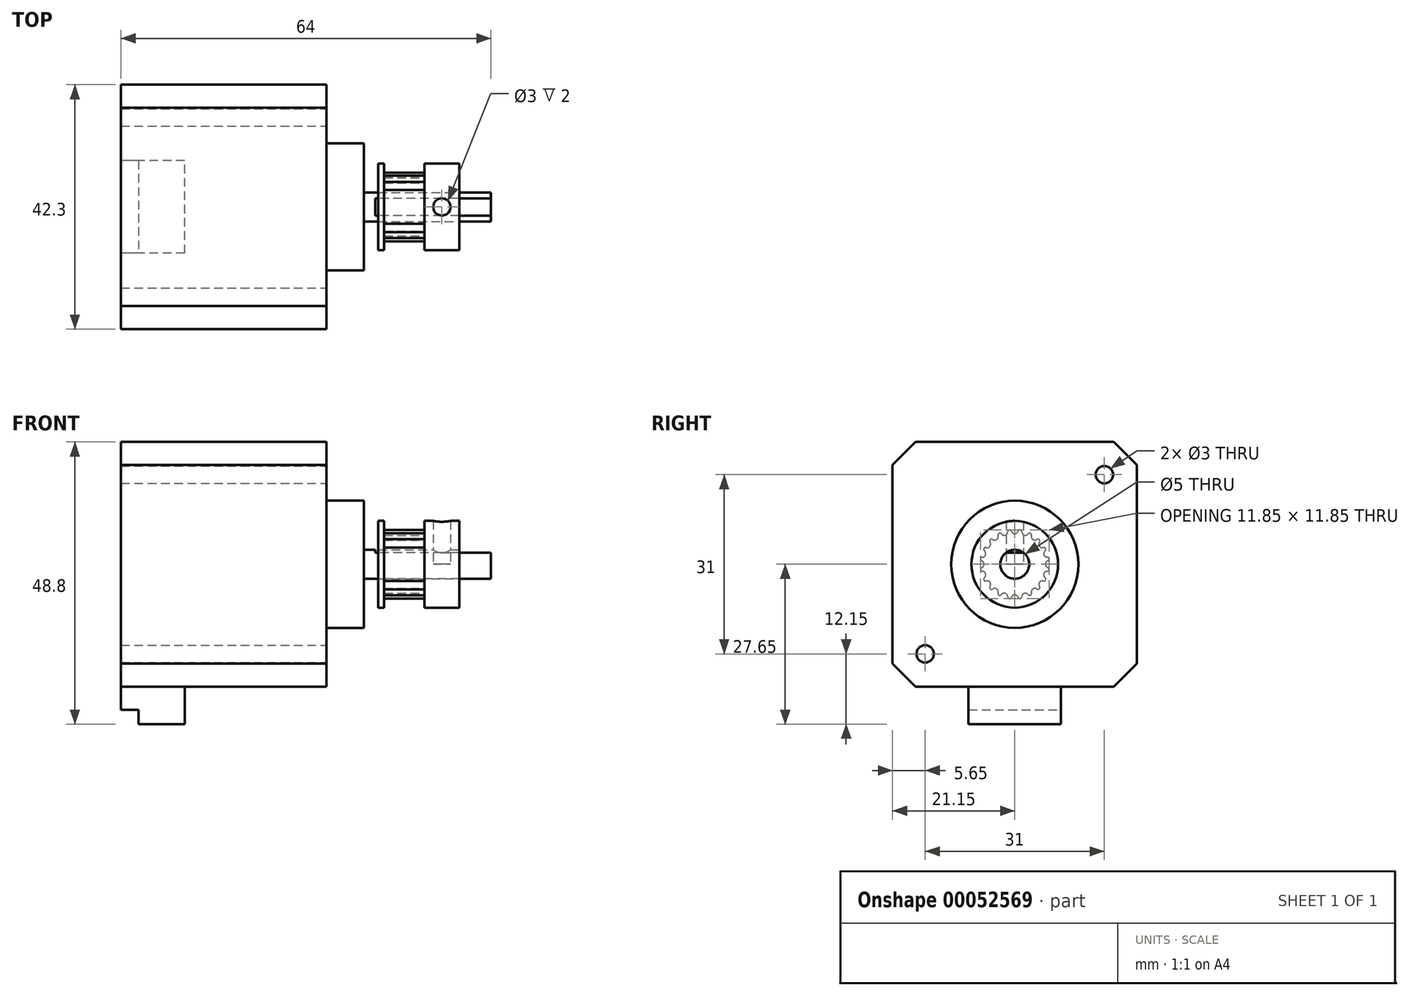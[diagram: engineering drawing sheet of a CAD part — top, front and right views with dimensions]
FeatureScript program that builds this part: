
annotation { "Feature Type Name" : "Feature", "Feature Type Description" : "" }
export const myFeature = defineFeature(function(context is Context, id is Id, definition is map)
    precondition{}
    {
        {
            var Q0;
            Q0=qCreatedBy(makeId("Right.planeOp"),FACE);
            var sketch = newSketch(context, id + "F0", { "sketchPlane" : qUnion([Q0])});
            skLineSegment(sketch, "E0", {"start": v(0, 0) * mm, "end": v(-19.15, 19.15) * mm, "construction": true});
            skLineSegment(sketch, "E1", {"start": v(-19.15, 19.15) * mm, "end": v(-17.15, 21.15) * mm});
            skLineSegment(sketch, "E2", {"start": v(-17.15, 21.15) * mm, "end": v(0, 21.15) * mm});
            skCircle(sketch, "E3", {"center": v(-15.5, 15.5) * mm, "radius": 1.5 * mm});
            skLineSegment(sketch, "E4.MirrorCS", {"start": v(-19.15, 19.15) * mm, "end": v(-21.15, 17.15) * mm});
            skLineSegment(sketch, "E5.MirrorCS", {"start": v(-21.15, 17.15) * mm, "end": v(-21.15, 0) * mm});
            skLineSegment(sketch, "E6.MirrorCS", {"start": v(17.15, 21.15) * mm, "end": v(0, 21.15) * mm});
            skCircle(sketch, "E7.MirrorC", {"center": v(15.5, 15.5) * mm, "radius": 1.5 * mm});
            skLineSegment(sketch, "E8.MirrorCS", {"start": v(19.15, 19.15) * mm, "end": v(17.15, 21.15) * mm});
            skLineSegment(sketch, "E9.MirrorCS", {"start": v(19.15, 19.15) * mm, "end": v(21.15, 17.15) * mm});
            skLineSegment(sketch, "E10.MirrorCS", {"start": v(21.15, 17.15) * mm, "end": v(21.15, 0) * mm});
            skLineSegment(sketch, "E11.MirrorCS", {"start": v(-21.15, -17.15) * mm, "end": v(-21.15, 0) * mm});
            skLineSegment(sketch, "E12.MirrorCS", {"start": v(-19.15, -19.15) * mm, "end": v(-21.15, -17.15) * mm});
            skLineSegment(sketch, "E13.MirrorCS", {"start": v(-19.15, -19.15) * mm, "end": v(-17.15, -21.15) * mm});
            skCircle(sketch, "E14.MirrorC", {"center": v(-15.5, -15.5) * mm, "radius": 1.5 * mm});
            skLineSegment(sketch, "E15.MirrorCS", {"start": v(-17.15, -21.15) * mm, "end": v(0, -21.15) * mm});
            skLineSegment(sketch, "E16.MirrorCS", {"start": v(17.15, -21.15) * mm, "end": v(0, -21.15) * mm});
            skLineSegment(sketch, "E17.MirrorCS", {"start": v(19.15, -19.15) * mm, "end": v(17.15, -21.15) * mm});
            skCircle(sketch, "E18.MirrorC", {"center": v(15.5, -15.5) * mm, "radius": 1.5 * mm});
            skLineSegment(sketch, "E19.MirrorCS", {"start": v(19.15, -19.15) * mm, "end": v(21.15, -17.15) * mm});
            skLineSegment(sketch, "E20.MirrorCS", {"start": v(21.15, -17.15) * mm, "end": v(21.15, 0) * mm});
            skCircle(sketch, "E21", {"center": v(0, 0) * mm, "radius": 11 * mm});
            skCircle(sketch, "E22", {"center": v(0, 0) * mm, "radius": 2.5 * mm});
            skLineSegment(sketch, "E23", {"start": v(-1.5, 2) * mm, "end": v(1.5, 2) * mm});
            skSolve(sketch);
        }
        {
            var Q0;
            {var subQ0=sQuery(id+"F0.wireOp",EDGE,"E23");Q0=makeQuery(id+"F0.imprint","IMPRINT",FACE,{"disambiguationData":[TD([[makeQuery(id+"F0.imprint","IMPRINT",EDGE,{"derivedFrom":subQ0}),1.0]])]});}
            var Q1;
            {var subQ0=sQuery(id+"F0.wireOp",EDGE,"E23");Q1=makeQuery(id+"F0.imprint","IMPRINT",FACE,{"disambiguationData":[TD([[makeQuery(id+"F0.imprint","IMPRINT",EDGE,{"derivedFrom":subQ0}),-1.0]])]});}
            var Q2;
            Q2=makeQuery(id+"F0.imprint","IMPRINT",FACE,{"disambiguationData":[TD([[makeQuery(id+"F0.imprint","IMPRINT",EDGE,{"derivedFrom":sQuery(id+"F0.wireOp",EDGE,"E21")}),1.0]])]});
            var Q3;
            Q3=makeQuery(id+"F0.imprint","IMPRINT",FACE,{"disambiguationData":[TD([[makeQuery(id+"F0.imprint","IMPRINT",EDGE,{"derivedFrom":sQuery(id+"F0.wireOp",EDGE,"E7.MirrorC")}),-1.0]])]});
            var Q4;
            Q4=makeQuery(id+"F0.imprint","IMPRINT",FACE,{"disambiguationData":[TD([[makeQuery(id+"F0.imprint","IMPRINT",EDGE,{"derivedFrom":sQuery(id+"F0.wireOp",EDGE,"E18.MirrorC")}),1.0]])]});
            var Q5;
            Q5=makeQuery(id+"F0.imprint","IMPRINT",FACE,{"disambiguationData":[TD([[makeQuery(id+"F0.imprint","IMPRINT",EDGE,{"derivedFrom":sQuery(id+"F0.wireOp",EDGE,"E14.MirrorC")}),-1.0]])]});
            var Q6;
            Q6=makeQuery(id+"F0.imprint","IMPRINT",FACE,{"disambiguationData":[TD([[makeQuery(id+"F0.imprint","IMPRINT",EDGE,{"derivedFrom":sQuery(id+"F0.wireOp",EDGE,"E3")}),1.0]])]});
            var Q7;
            Q7=makeQuery(id+"F0.imprint","IMPRINT",FACE,{"disambiguationData":[TD([[makeQuery(id+"F0.imprint","IMPRINT",EDGE,{"derivedFrom":sQuery(id+"F0.wireOp",EDGE,"E1")}),-1.0]])]});
            extrude(context, id + "F1", {"entities" : qUnion([Q0, Q1, Q2, Q3, Q4, Q5, Q6, Q7]), "oppositeDirection" : true, "depth" : 40 * mm});
        }
        {
            var Q0;
            {var subQ0=sQuery(id+"F0.wireOp",EDGE,"E23");Q0=makeQuery(id+"F0.imprint","IMPRINT",FACE,{"disambiguationData":[TD([[makeQuery(id+"F0.imprint","IMPRINT",EDGE,{"derivedFrom":subQ0}),-1.0]])]});}
            extrude(context, id + "F2", {"entities" : qUnion([Q0]), "operationType" : NewBodyOperationType.ADD, "depth" : 24 * mm});
        }
        {
            var Q0;
            {var subQ0=sQuery(id+"F0.wireOp",EDGE,"E23");Q0=makeQuery(id+"F0.imprint","IMPRINT",FACE,{"disambiguationData":[TD([[makeQuery(id+"F0.imprint","IMPRINT",EDGE,{"derivedFrom":subQ0}),1.0]])]});}
            extrude(context, id + "F3", {"entities" : qUnion([Q0]), "operationType" : NewBodyOperationType.ADD, "depth" : 4 * mm});
        }
        {
            var Q0;
            Q0=makeQuery(id+"F0.imprint","IMPRINT",FACE,{"disambiguationData":[TD([[makeQuery(id+"F0.imprint","IMPRINT",EDGE,{"derivedFrom":sQuery(id+"F0.wireOp",EDGE,"E21")}),1.0]])]});
            extrude(context, id + "F4", {"entities" : qUnion([Q0]), "operationType" : NewBodyOperationType.ADD, "depth" : 2 * mm});
        }
        {
            var Q0;
            Q0=makeQuery(id+"F0.imprint","IMPRINT",FACE,{"disambiguationData":[TD([[makeQuery(id+"F0.imprint","IMPRINT",EDGE,{"derivedFrom":sQuery(id+"F0.wireOp",EDGE,"E3")}),1.0]])]});
            var Q1;
            Q1=makeQuery(id+"F0.imprint","IMPRINT",FACE,{"disambiguationData":[TD([[makeQuery(id+"F0.imprint","IMPRINT",EDGE,{"derivedFrom":sQuery(id+"F0.wireOp",EDGE,"E7.MirrorC")}),-1.0]])]});
            var Q2;
            Q2=makeQuery(id+"F0.imprint","IMPRINT",FACE,{"disambiguationData":[TD([[makeQuery(id+"F0.imprint","IMPRINT",EDGE,{"derivedFrom":sQuery(id+"F0.wireOp",EDGE,"E18.MirrorC")}),1.0]])]});
            var Q3;
            Q3=makeQuery(id+"F0.imprint","IMPRINT",FACE,{"disambiguationData":[TD([[makeQuery(id+"F0.imprint","IMPRINT",EDGE,{"derivedFrom":sQuery(id+"F0.wireOp",EDGE,"E14.MirrorC")}),-1.0]])]});
            extrude(context, id + "F5", {"entities" : qUnion([Q0, Q1, Q2, Q3]), "operationType" : NewBodyOperationType.REMOVE, "oppositeDirection" : true, "depth" : 4.5 * mm});
        }
        {
            var Q0;
            Q0=makeQuery(id+"F1.opExtrude","CAP_FACE",FACE,{"disambiguationData":[OSD([sQuery(id+"F0.wireOp",EDGE,"E1"),sQuery(id+"F0.wireOp",EDGE,"E2"),sQuery(id+"F0.wireOp",EDGE,"E4.MirrorCS"),sQuery(id+"F0.wireOp",EDGE,"E5.MirrorCS"),sQuery(id+"F0.wireOp",EDGE,"E6.MirrorCS"),sQuery(id+"F0.wireOp",EDGE,"E8.MirrorCS"),sQuery(id+"F0.wireOp",EDGE,"E9.MirrorCS"),sQuery(id+"F0.wireOp",EDGE,"E10.MirrorCS"),sQuery(id+"F0.wireOp",EDGE,"E11.MirrorCS"),sQuery(id+"F0.wireOp",EDGE,"E12.MirrorCS"),sQuery(id+"F0.wireOp",EDGE,"E13.MirrorCS"),sQuery(id+"F0.wireOp",EDGE,"E15.MirrorCS"),sQuery(id+"F0.wireOp",EDGE,"E16.MirrorCS"),sQuery(id+"F0.wireOp",EDGE,"E17.MirrorCS"),sQuery(id+"F0.wireOp",EDGE,"E19.MirrorCS"),sQuery(id+"F0.wireOp",EDGE,"E20.MirrorCS")])],"isStart":false});
            var sketch = newSketch(context, id + "F6", { "sketchPlane" : qUnion([Q0])});
            skLineSegment(sketch, "E24", {"start": v(-8, -21.15) * mm, "end": v(-8, -27.65) * mm});
            skLineSegment(sketch, "E25.MirrorCS", {"start": v(8, -21.15) * mm, "end": v(8, -27.65) * mm});
            skLineSegment(sketch, "E26", {"start": v(-8, -27.65) * mm, "end": v(8, -27.65) * mm});
            skLineSegment(sketch, "E27", {"start": v(-8, -21.15) * mm, "end": v(8, -21.15) * mm});
            skLineSegment(sketch, "E28", {"start": v(8, -25.15) * mm, "end": v(-8, -25.15) * mm});
            skSolve(sketch);
        }
        {
            var Q0;
            {var subQ0=sQuery(id+"F6.wireOp",EDGE,"E27");Q0=makeQuery(id+"F6.imprint","IMPRINT",FACE,{"disambiguationData":[TD([[makeQuery(id+"F6.imprint","IMPRINT",EDGE,{"derivedFrom":subQ0}),1.0]])]});}
            var Q1;
            {var subQ1=sQuery(id+"F6.wireOp",EDGE,"E26");Q1=makeQuery(id+"F6.imprint","IMPRINT",FACE,{"disambiguationData":[TD([[makeQuery(id+"F6.imprint","IMPRINT",EDGE,{"derivedFrom":subQ1}),1.0]])]});}
            extrude(context, id + "F7", {"entities" : qUnion([Q0, Q1]), "operationType" : NewBodyOperationType.ADD, "oppositeDirection" : true, "depth" : 11 * mm});
        }
        {
            var Q0;
            {var subQ1=sQuery(id+"F6.wireOp",EDGE,"E26");Q0=makeQuery(id+"F6.imprint","IMPRINT",FACE,{"disambiguationData":[TD([[makeQuery(id+"F6.imprint","IMPRINT",EDGE,{"derivedFrom":subQ1}),1.0]])]});}
            extrude(context, id + "F8", {"entities" : qUnion([Q0]), "operationType" : NewBodyOperationType.REMOVE, "oppositeDirection" : true, "depth" : 3 * mm});
        }
        {
            var Q0;
            Q0=qCreatedBy(makeId("Right.planeOp"),FACE);
            cPlane(context, id + "F9", {"entities" : qUnion([Q0]), "cplaneType" : CPlaneType.OFFSET, "offset" : 9 * mm, "width" : 150 * mm, "height" : 150 * mm});
        }
        {
            var Q0;
            Q0=qCreatedBy(id+"F9.planeOp",FACE);
            var sketch = newSketch(context, id + "F10", { "sketchPlane" : qUnion([Q0])});
            skCircle(sketch, "E29", {"center": v(0, 0) * mm, "radius": 7.5 * mm});
            skCircle(sketch, "E30", {"center": v(0, 0) * mm, "radius": 2.5 * mm});
            skSolve(sketch);
        }
        {
            var Q0;
            Q0=makeQuery(id+"F10.imprint","IMPRINT",FACE,{"disambiguationData":[TD([[makeQuery(id+"F10.imprint","IMPRINT",EDGE,{"derivedFrom":sQuery(id+"F10.wireOp",EDGE,"E29")}),1.0]])]});
            extrude(context, id + "F11", {"entities" : qUnion([Q0]), "oppositeDirection" : true, "depth" : 4.5 * mm, "hasSecondDirection" : true, "secondDirectionOppositeDirection" : false, "secondDirectionDepth" : 9.5 * mm});
        }
        {
            var Q0;
            Q0=qCreatedBy(id+"F9.planeOp",FACE);
            var sketch = newSketch(context, id + "F12", { "sketchPlane" : qUnion([Q0])});
            skArc(sketch, "E31", {"start": v(-0.57, 5.7) * mm, "mid": v(0, 5.3) * mm, "end": v(0.57, 5.7) * mm});
            skArc(sketch, "E32", {"start": v(0.94, 5.93) * mm, "mid": v(0.71, 5.88) * mm, "end": v(0.57, 5.7) * mm});
            skLineSegment(sketch, "E33", {"start": v(0, 5.9) * mm, "end": v(0, 0) * mm, "construction": true});
            skLineSegment(sketch, "E34", {"start": v(0, 0) * mm, "end": v(0.94, 5.93) * mm, "construction": true});
            skArc(sketch, "E35.MirrorCS", {"start": v(-0.94, 5.93) * mm, "mid": v(-0.71, 5.88) * mm, "end": v(-0.57, 5.7) * mm});
            skArc(sketch, "E36.1.0", {"start": v(2.72, 5.35) * mm, "mid": v(2.5, 5.37) * mm, "end": v(2.3, 5.25) * mm});
            skArc(sketch, "E36.1.1", {"start": v(1.22, 5.6) * mm, "mid": v(1.64, 5.04) * mm, "end": v(2.3, 5.25) * mm});
            skArc(sketch, "E36.1.2", {"start": v(0.94, 5.93) * mm, "mid": v(1.14, 5.81) * mm, "end": v(1.22, 5.6) * mm});
            skArc(sketch, "E36.2.0", {"start": v(4.24, 4.24) * mm, "mid": v(4.03, 4.34) * mm, "end": v(3.81, 4.28) * mm});
            skArc(sketch, "E36.2.1", {"start": v(2.9, 4.95) * mm, "mid": v(3.12, 4.29) * mm, "end": v(3.81, 4.28) * mm});
            skArc(sketch, "E36.2.2", {"start": v(2.72, 5.35) * mm, "mid": v(2.88, 5.18) * mm, "end": v(2.9, 4.95) * mm});
            skArc(sketch, "E36.3.0", {"start": v(5.35, 2.72) * mm, "mid": v(5.18, 2.88) * mm, "end": v(4.95, 2.9) * mm});
            skArc(sketch, "E36.3.1", {"start": v(4.28, 3.81) * mm, "mid": v(4.29, 3.12) * mm, "end": v(4.95, 2.9) * mm});
            skArc(sketch, "E36.3.2", {"start": v(4.24, 4.24) * mm, "mid": v(4.34, 4.03) * mm, "end": v(4.28, 3.81) * mm});
            skArc(sketch, "E36.4.0", {"start": v(5.93, 0.94) * mm, "mid": v(5.81, 1.14) * mm, "end": v(5.6, 1.22) * mm});
            skArc(sketch, "E36.4.1", {"start": v(5.25, 2.3) * mm, "mid": v(5.04, 1.64) * mm, "end": v(5.6, 1.22) * mm});
            skArc(sketch, "E36.4.2", {"start": v(5.35, 2.72) * mm, "mid": v(5.37, 2.5) * mm, "end": v(5.25, 2.3) * mm});
            skArc(sketch, "E36.5.0", {"start": v(5.93, -0.94) * mm, "mid": v(5.88, -0.71) * mm, "end": v(5.7, -0.57) * mm});
            skArc(sketch, "E36.5.1", {"start": v(5.7, 0.57) * mm, "mid": v(5.3, 0) * mm, "end": v(5.7, -0.57) * mm});
            skArc(sketch, "E36.5.2", {"start": v(5.93, 0.94) * mm, "mid": v(5.88, 0.71) * mm, "end": v(5.7, 0.57) * mm});
            skArc(sketch, "E36.6.0", {"start": v(5.35, -2.72) * mm, "mid": v(5.37, -2.5) * mm, "end": v(5.25, -2.3) * mm});
            skArc(sketch, "E36.6.1", {"start": v(5.6, -1.22) * mm, "mid": v(5.04, -1.64) * mm, "end": v(5.25, -2.3) * mm});
            skArc(sketch, "E36.6.2", {"start": v(5.93, -0.94) * mm, "mid": v(5.81, -1.14) * mm, "end": v(5.6, -1.22) * mm});
            skArc(sketch, "E36.7.0", {"start": v(4.24, -4.24) * mm, "mid": v(4.34, -4.03) * mm, "end": v(4.28, -3.81) * mm});
            skArc(sketch, "E36.7.1", {"start": v(4.95, -2.9) * mm, "mid": v(4.29, -3.12) * mm, "end": v(4.28, -3.81) * mm});
            skArc(sketch, "E36.7.2", {"start": v(5.35, -2.72) * mm, "mid": v(5.18, -2.88) * mm, "end": v(4.95, -2.9) * mm});
            skArc(sketch, "E36.8.0", {"start": v(2.72, -5.35) * mm, "mid": v(2.88, -5.18) * mm, "end": v(2.9, -4.95) * mm});
            skArc(sketch, "E36.8.1", {"start": v(3.81, -4.28) * mm, "mid": v(3.12, -4.29) * mm, "end": v(2.9, -4.95) * mm});
            skArc(sketch, "E36.8.2", {"start": v(4.24, -4.24) * mm, "mid": v(4.03, -4.34) * mm, "end": v(3.81, -4.28) * mm});
            skArc(sketch, "E36.9.0", {"start": v(0.94, -5.93) * mm, "mid": v(1.14, -5.81) * mm, "end": v(1.22, -5.6) * mm});
            skArc(sketch, "E36.9.1", {"start": v(2.3, -5.25) * mm, "mid": v(1.64, -5.04) * mm, "end": v(1.22, -5.6) * mm});
            skArc(sketch, "E36.9.2", {"start": v(2.72, -5.35) * mm, "mid": v(2.5, -5.37) * mm, "end": v(2.3, -5.25) * mm});
            skArc(sketch, "E36.10.0", {"start": v(-0.94, -5.93) * mm, "mid": v(-0.71, -5.88) * mm, "end": v(-0.57, -5.7) * mm});
            skArc(sketch, "E36.10.1", {"start": v(0.57, -5.7) * mm, "mid": v(0, -5.3) * mm, "end": v(-0.57, -5.7) * mm});
            skArc(sketch, "E36.10.2", {"start": v(0.94, -5.93) * mm, "mid": v(0.71, -5.88) * mm, "end": v(0.57, -5.7) * mm});
            skArc(sketch, "E36.11.0", {"start": v(-2.72, -5.35) * mm, "mid": v(-2.5, -5.37) * mm, "end": v(-2.3, -5.25) * mm});
            skArc(sketch, "E36.11.1", {"start": v(-1.22, -5.6) * mm, "mid": v(-1.64, -5.04) * mm, "end": v(-2.3, -5.25) * mm});
            skArc(sketch, "E36.11.2", {"start": v(-0.94, -5.93) * mm, "mid": v(-1.14, -5.81) * mm, "end": v(-1.22, -5.6) * mm});
            skArc(sketch, "E36.12.0", {"start": v(-4.24, -4.24) * mm, "mid": v(-4.03, -4.34) * mm, "end": v(-3.81, -4.28) * mm});
            skArc(sketch, "E36.12.1", {"start": v(-2.9, -4.95) * mm, "mid": v(-3.12, -4.29) * mm, "end": v(-3.81, -4.28) * mm});
            skArc(sketch, "E36.12.2", {"start": v(-2.72, -5.35) * mm, "mid": v(-2.88, -5.18) * mm, "end": v(-2.9, -4.95) * mm});
            skArc(sketch, "E36.13.0", {"start": v(-5.35, -2.72) * mm, "mid": v(-5.18, -2.88) * mm, "end": v(-4.95, -2.9) * mm});
            skArc(sketch, "E36.13.1", {"start": v(-4.28, -3.81) * mm, "mid": v(-4.29, -3.12) * mm, "end": v(-4.95, -2.9) * mm});
            skArc(sketch, "E36.13.2", {"start": v(-4.24, -4.24) * mm, "mid": v(-4.34, -4.03) * mm, "end": v(-4.28, -3.81) * mm});
            skArc(sketch, "E36.14.0", {"start": v(-5.93, -0.94) * mm, "mid": v(-5.81, -1.14) * mm, "end": v(-5.6, -1.22) * mm});
            skArc(sketch, "E36.14.1", {"start": v(-5.25, -2.3) * mm, "mid": v(-5.04, -1.64) * mm, "end": v(-5.6, -1.22) * mm});
            skArc(sketch, "E36.14.2", {"start": v(-5.35, -2.72) * mm, "mid": v(-5.37, -2.5) * mm, "end": v(-5.25, -2.3) * mm});
            skArc(sketch, "E36.15.0", {"start": v(-5.93, 0.94) * mm, "mid": v(-5.88, 0.71) * mm, "end": v(-5.7, 0.57) * mm});
            skArc(sketch, "E36.15.1", {"start": v(-5.7, -0.57) * mm, "mid": v(-5.3, 0) * mm, "end": v(-5.7, 0.57) * mm});
            skArc(sketch, "E36.15.2", {"start": v(-5.93, -0.94) * mm, "mid": v(-5.88, -0.71) * mm, "end": v(-5.7, -0.57) * mm});
            skArc(sketch, "E36.16.0", {"start": v(-5.35, 2.72) * mm, "mid": v(-5.37, 2.5) * mm, "end": v(-5.25, 2.3) * mm});
            skArc(sketch, "E36.16.1", {"start": v(-5.6, 1.22) * mm, "mid": v(-5.04, 1.64) * mm, "end": v(-5.25, 2.3) * mm});
            skArc(sketch, "E36.16.2", {"start": v(-5.93, 0.94) * mm, "mid": v(-5.81, 1.14) * mm, "end": v(-5.6, 1.22) * mm});
            skArc(sketch, "E36.17.0", {"start": v(-4.24, 4.24) * mm, "mid": v(-4.34, 4.03) * mm, "end": v(-4.28, 3.81) * mm});
            skArc(sketch, "E36.17.1", {"start": v(-4.95, 2.9) * mm, "mid": v(-4.29, 3.12) * mm, "end": v(-4.28, 3.81) * mm});
            skArc(sketch, "E36.17.2", {"start": v(-5.35, 2.72) * mm, "mid": v(-5.18, 2.88) * mm, "end": v(-4.95, 2.9) * mm});
            skArc(sketch, "E36.18.0", {"start": v(-2.72, 5.35) * mm, "mid": v(-2.88, 5.18) * mm, "end": v(-2.9, 4.95) * mm});
            skArc(sketch, "E36.18.1", {"start": v(-3.81, 4.28) * mm, "mid": v(-3.12, 4.29) * mm, "end": v(-2.9, 4.95) * mm});
            skArc(sketch, "E36.18.2", {"start": v(-4.24, 4.24) * mm, "mid": v(-4.03, 4.34) * mm, "end": v(-3.81, 4.28) * mm});
            skArc(sketch, "E36.19.0", {"start": v(-0.94, 5.93) * mm, "mid": v(-1.14, 5.81) * mm, "end": v(-1.22, 5.6) * mm});
            skArc(sketch, "E36.19.1", {"start": v(-2.3, 5.25) * mm, "mid": v(-1.64, 5.04) * mm, "end": v(-1.22, 5.6) * mm});
            skArc(sketch, "E36.19.2", {"start": v(-2.72, 5.35) * mm, "mid": v(-2.5, 5.37) * mm, "end": v(-2.3, 5.25) * mm});
            skPoint(sketch, "E36.center", {"position": v(0, 0) * mm});
            skLineSegment(sketch, "E36.anchor1", {"start": v(0, 0) * mm, "end": v(0.57, 5.7) * mm, "construction": true});
            skLineSegment(sketch, "E36.anchor2", {"start": v(0, 0) * mm, "end": v(-1.22, 5.6) * mm, "construction": true});
            skCircle(sketch, "E37", {"center": v(0, 0) * mm, "radius": 7.5 * mm});
            skSolve(sketch);
        }
        {
            var Q0;
            Q0=makeQuery(id+"F12.imprint","IMPRINT",FACE,{"disambiguationData":[TD([[makeQuery(id+"F12.imprint","IMPRINT",EDGE,{"derivedFrom":sQuery(id+"F12.wireOp",EDGE,"E31")}),1.0]])]});
            extrude(context, id + "F13", {"entities" : qUnion([Q0]), "operationType" : NewBodyOperationType.REMOVE, "endBound" : BoundingType.SYMMETRIC, "oppositeDirection" : true, "depth" : 7 * mm});
        }
        {
            var Q0;
            Q0=qCreatedBy(makeId("Top.planeOp"),FACE);
            var sketch = newSketch(context, id + "F14", { "sketchPlane" : qUnion([Q0])});
            skCircle(sketch, "E38", {"center": v(15.5, 0) * mm, "radius": 1.5 * mm});
            skSolve(sketch);
        }
        {
            var Q0;
            Q0=makeQuery(id+"F14.imprint","IMPRINT",FACE,{"disambiguationData":[TD([[makeQuery(id+"F14.imprint","IMPRINT",EDGE,{"derivedFrom":sQuery(id+"F14.wireOp",EDGE,"E38")}),1.0]])]});
            extrude(context, id + "F15", {"entities" : qUnion([Q0]), "operationType" : NewBodyOperationType.REMOVE, "depth" : 25 * mm});
        }
    });
